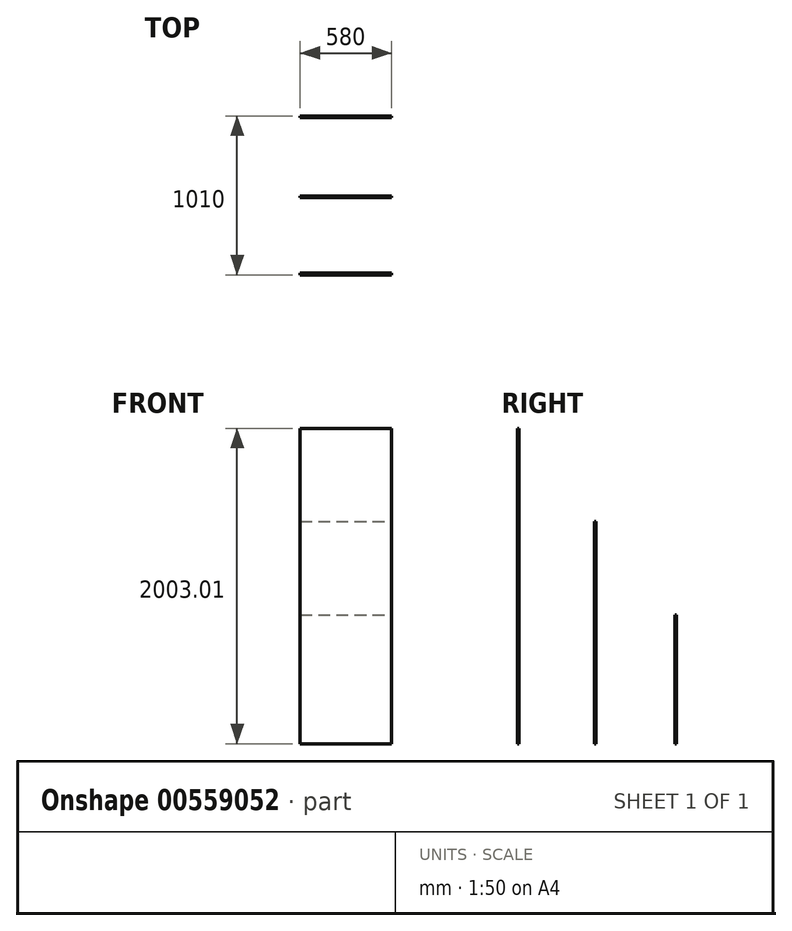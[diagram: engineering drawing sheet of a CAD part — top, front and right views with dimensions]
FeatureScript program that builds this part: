
annotation { "Feature Type Name" : "Feature", "Feature Type Description" : "" }
export const myFeature = defineFeature(function(context is Context, id is Id, definition is map)
    precondition{}
    {
        {
            var Q0;
            Q0=qCreatedBy(makeId("Right.planeOp"),FACE);
            var sketch = newSketch(context, id + "F0", { "sketchPlane" : qUnion([Q0])});
            skLineSegment(sketch, "E0", {"start": v(2335, 0) * mm, "end": v(0, 0) * mm});
            skLineSegment(sketch, "E1", {"start": v(0, 0) * mm, "end": v(0, 2450) * mm});
            skLineSegment(sketch, "E2", {"start": v(0, 2450) * mm, "end": v(690, 2450) * mm});
            skLineSegment(sketch, "E3", {"start": v(690, 2450) * mm, "end": v(2335, 500) * mm});
            skLineSegment(sketch, "E4", {"start": v(2335, 500) * mm, "end": v(2335, 0) * mm});
            skLineSegment(sketch, "E5", {"start": v(362.93, 2450) * mm, "end": v(2335, 112.28) * mm});
            skLineSegment(sketch, "E6", {"start": v(2335, 112.28) * mm, "end": v(362.93, 2450) * mm});
            skLineSegment(sketch, "E7.bottom", {"start": v(70, 0) * mm, "end": v(670, 0) * mm});
            skLineSegment(sketch, "E7.top", {"start": v(70, 1830) * mm, "end": v(670, 1830) * mm});
            skLineSegment(sketch, "E7.left", {"start": v(70, 0) * mm, "end": v(70, 1830) * mm});
            skLineSegment(sketch, "E7.right", {"start": v(670, 0) * mm, "end": v(670, 1830) * mm});
            skLineSegment(sketch, "E8", {"start": v(0, 1900) * mm, "end": v(740, 1900) * mm});
            skLineSegment(sketch, "E9", {"start": v(740, 1900) * mm, "end": v(740, 1900) * mm});
            skLineSegment(sketch, "E10", {"start": v(740, 0) * mm, "end": v(740, 1900) * mm});
            skLineSegment(sketch, "E11.bottom", {"start": v(720, 980) * mm, "end": v(1180, 980) * mm});
            skLineSegment(sketch, "E11.top", {"start": v(720, 330) * mm, "end": v(1180, 330) * mm});
            skLineSegment(sketch, "E11.left", {"start": v(720, 980) * mm, "end": v(720, 330) * mm});
            skLineSegment(sketch, "E11.right", {"start": v(1180, 980) * mm, "end": v(1180, 330) * mm});
            skSolve(sketch);
        }
        {
            var Q0;
            Q0=qCreatedBy(makeId("Right.planeOp"),FACE);
            var sketch = newSketch(context, id + "F1", { "sketchPlane" : qUnion([Q0])});
            skLineSegment(sketch, "E12.bottom", {"start": v(740, 0) * mm, "end": v(1240, 0) * mm});
            skLineSegment(sketch, "E12.left", {"start": v(740, 0) * mm, "end": v(740, 2003.01) * mm});
            skLineSegment(sketch, "E12.right", {"start": v(1240, 0) * mm, "end": v(1240, 1410.3) * mm});
            skLineSegment(sketch, "E13.bottom", {"start": v(1240, 0) * mm, "end": v(1740, 0) * mm});
            skLineSegment(sketch, "E14.top", {"start": v(2240, 0) * mm, "end": v(1740, 0) * mm});
            skLineSegment(sketch, "E14.left", {"start": v(2240, 224.9) * mm, "end": v(2240, 0) * mm});
            skLineSegment(sketch, "E14.right", {"start": v(1740, 817.6) * mm, "end": v(1740, 0) * mm});
            skLineSegment(sketch, "E15", {"start": v(1240, 1410.3) * mm, "end": v(740, 2003.01) * mm});
            skLineSegment(sketch, "E16", {"start": v(1240, 1410.3) * mm, "end": v(1740, 817.6) * mm});
            skLineSegment(sketch, "E17", {"start": v(2240, 224.9) * mm, "end": v(1740, 817.6) * mm});
            skLineSegment(sketch, "E18", {"start": v(740, 50) * mm, "end": v(2240, 50) * mm});
            skSolve(sketch);
        }
        {
            var Q0;
            Q0=qCreatedBy(makeId("Right.planeOp"),FACE);
            var sketch = newSketch(context, id + "F2", { "sketchPlane" : qUnion([Q0])});
            skLineSegment(sketch, "E19.bottom", {"start": v(740, 0) * mm, "end": v(750, 0) * mm});
            skLineSegment(sketch, "E19.top", {"start": v(740, 2003.01) * mm, "end": v(750, 2003.01) * mm});
            skLineSegment(sketch, "E19.left", {"start": v(740, 0) * mm, "end": v(740, 2003.01) * mm});
            skLineSegment(sketch, "E19.right", {"start": v(750, 0) * mm, "end": v(750, 2003.01) * mm});
            skLineSegment(sketch, "E20.bottom", {"start": v(1240, 0) * mm, "end": v(1230, 0) * mm});
            skLineSegment(sketch, "E20.top", {"start": v(1240, 1410.3) * mm, "end": v(1230, 1410.3) * mm});
            skLineSegment(sketch, "E20.left", {"start": v(1240, 0) * mm, "end": v(1240, 1410.3) * mm});
            skLineSegment(sketch, "E20.right", {"start": v(1230, 0) * mm, "end": v(1230, 1410.3) * mm});
            skLineSegment(sketch, "E21.bottom", {"start": v(1740, 0) * mm, "end": v(1750, 0) * mm});
            skLineSegment(sketch, "E21.top", {"start": v(1740, 817.6) * mm, "end": v(1750, 817.6) * mm});
            skLineSegment(sketch, "E21.left", {"start": v(1740, 0) * mm, "end": v(1740, 817.6) * mm});
            skLineSegment(sketch, "E21.right", {"start": v(1750, 0) * mm, "end": v(1750, 817.6) * mm});
            skSolve(sketch);
        }
        {
            var Q0;
            Q0 = qSketchRegion(id + "F2", true);
            extrude(context, id + "F3", {"entities" : qUnion([Q0]), "oppositeDirection" : true, "depth" : 580 * mm, "offsetDistance" : 25 * mm});
        }
    });
